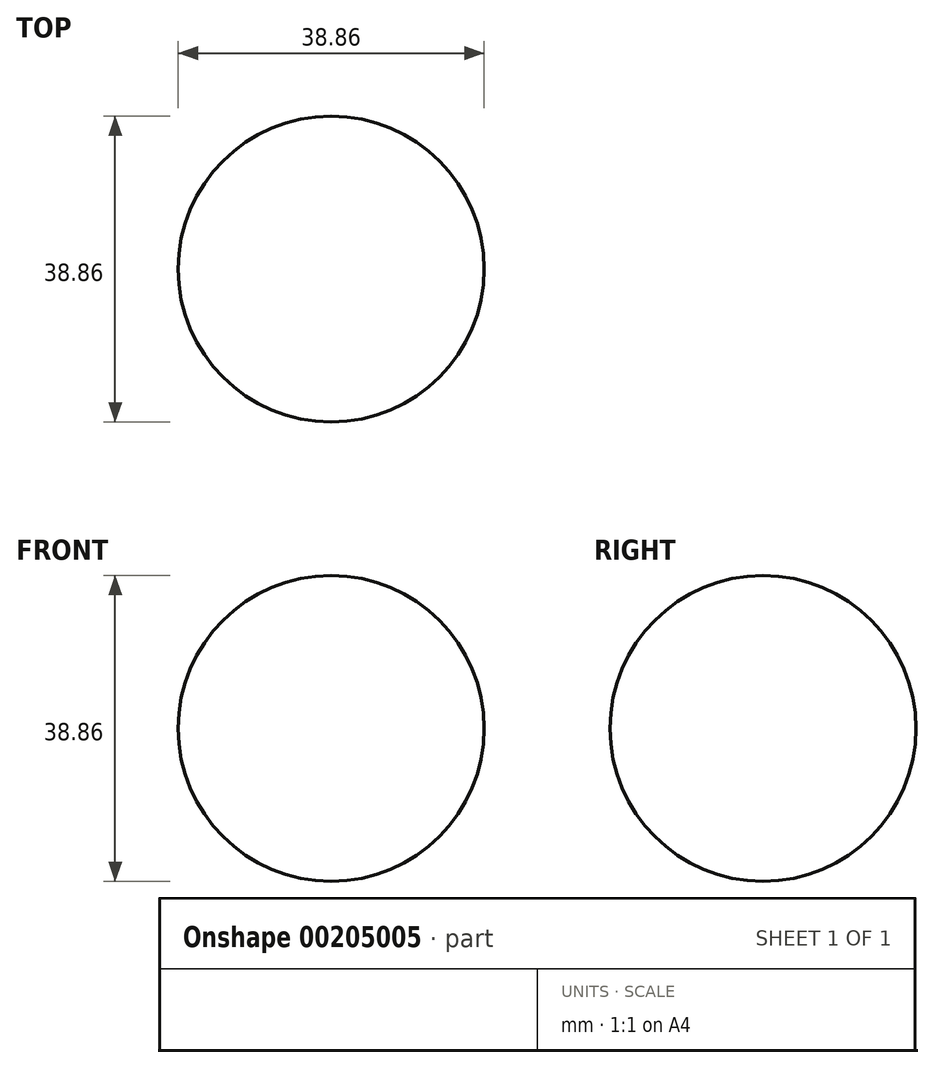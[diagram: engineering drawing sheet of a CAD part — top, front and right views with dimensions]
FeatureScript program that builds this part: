
annotation { "Feature Type Name" : "Feature", "Feature Type Description" : "" }
export const myFeature = defineFeature(function(context is Context, id is Id, definition is map)
    precondition{}
    {
        {
            var Q0;
            Q0=qCreatedBy(makeId("Top.planeOp"),FACE);
            var sketch = newSketch(context, id + "F0", { "sketchPlane" : qUnion([Q0])});
            skCircle(sketch, "E0", {"center": v(0, 0) * mm, "radius": 19.43 * mm});
            skLineSegment(sketch, "E1", {"start": v(0, 0) * mm, "end": v(0, 19.43) * mm});
            skLineSegment(sketch, "E2", {"start": v(0, 19.43) * mm, "end": v(0, -19.43) * mm});
            skSolve(sketch);
        }
        {
            var Q0;
            {var subQ0=sQuery(id+"F0.wireOp",EDGE,"E2");var subQ4=makeQuery(id+"F0.imprint","IMPRINT",VERTEX,{"derivedFrom":subQ0});Q0=makeQuery(id+"F0.imprint","IMPRINT",FACE,{"disambiguationData":[TD([[makeQuery(id+"F0.imprint","IMPRINT",EDGE,{"disambiguationData":[TD([[subQ4,1.0]])],"derivedFrom":subQ0}),1.0]])]});}
            var Q1;
            Q1=sQuery(id+"F0.wireOp",EDGE,"E2");
            revolve(context, id + "F1", {"entities" : qUnion([Q0]), "axis" : qUnion([Q1]), "revolveType" : RevolveType.FULL});
        }
    });
